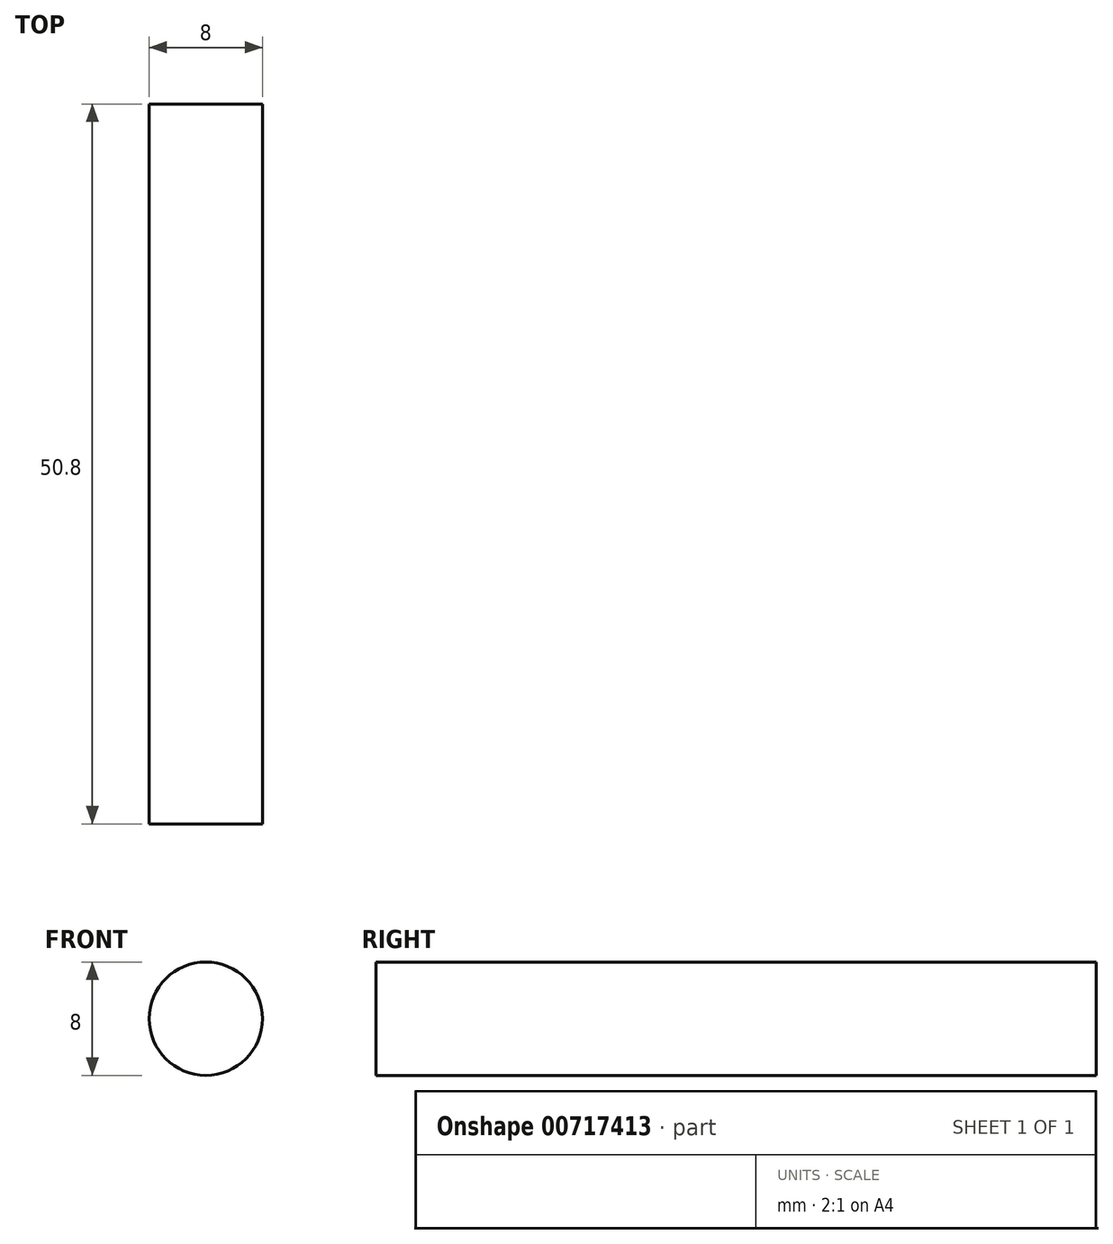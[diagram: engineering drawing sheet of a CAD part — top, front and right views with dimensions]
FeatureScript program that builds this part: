
annotation { "Feature Type Name" : "Feature", "Feature Type Description" : "" }
export const myFeature = defineFeature(function(context is Context, id is Id, definition is map)
    precondition{}
    {
        {
            var Q0;
            Q0=qCreatedBy(makeId("Front.planeOp"),FACE);
            var sketch = newSketch(context, id + "F0", { "sketchPlane" : qUnion([Q0])});
            skCircle(sketch, "E0", {"center": v(0, 0) * mm, "radius": 4 * mm});
            skSolve(sketch);
        }
        {
            var Q0;
            Q0 = qSketchRegion(id + "F0", true);
            extrude(context, id + "F1", {"entities" : qUnion([Q0]), "depth" : 50.8 * mm, "offsetDistance" : 25.4 * mm});
        }
    });
